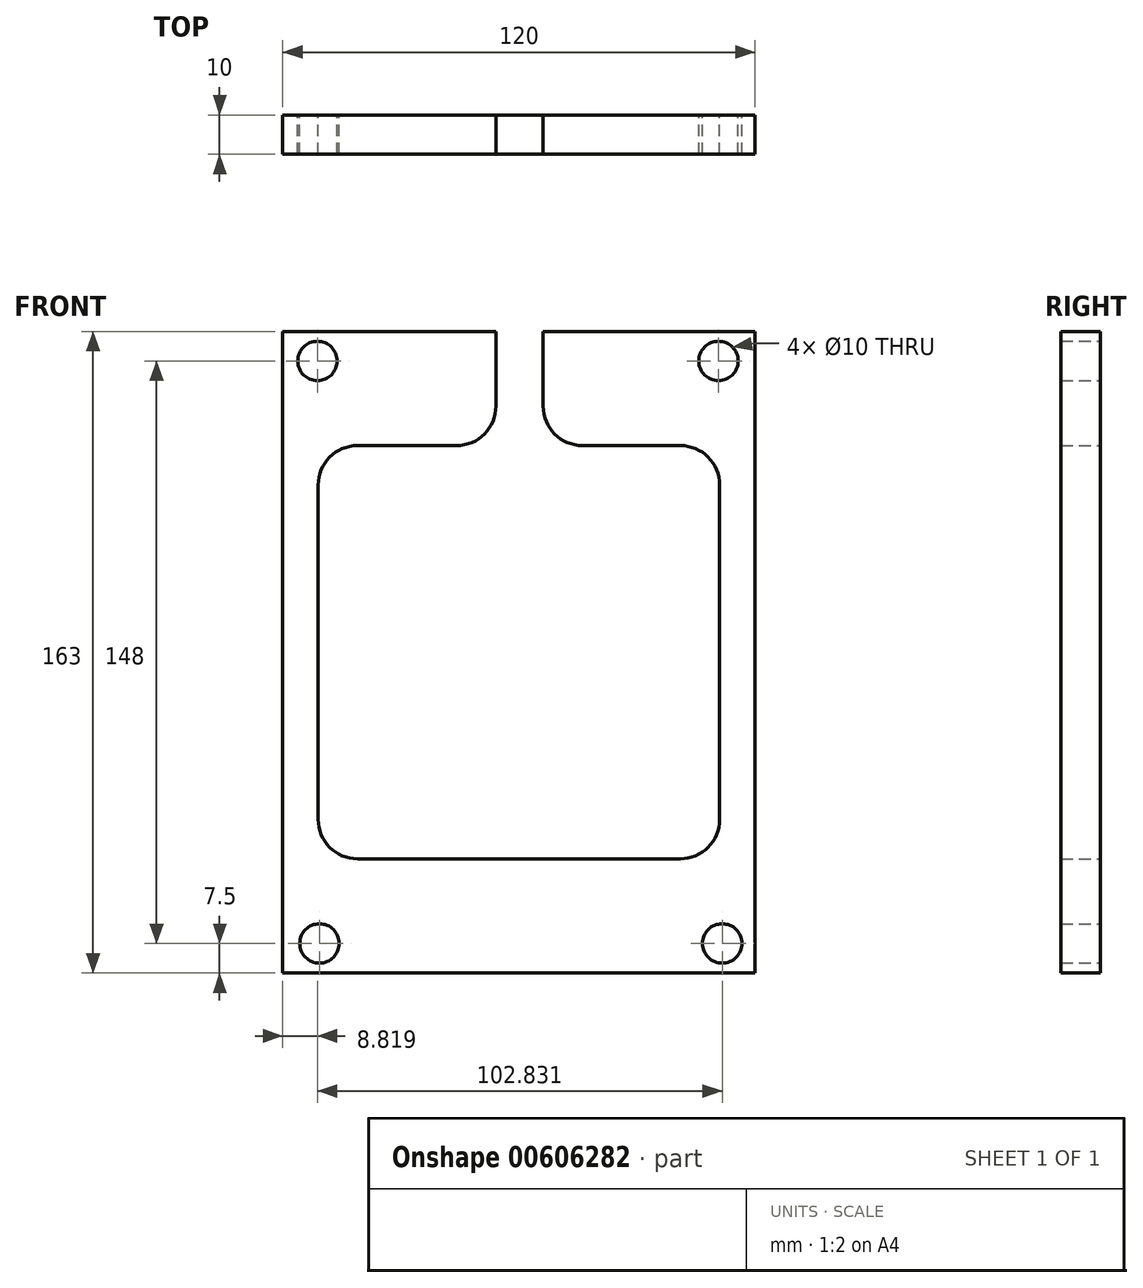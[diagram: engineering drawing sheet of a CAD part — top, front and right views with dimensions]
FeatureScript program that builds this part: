
annotation { "Feature Type Name" : "Feature", "Feature Type Description" : "" }
export const myFeature = defineFeature(function(context is Context, id is Id, definition is map)
    precondition{}
    {
        {
            var Q0;
            Q0=qCreatedBy(makeId("Front.planeOp"),FACE);
            var sketch = newSketch(context, id + "F0", { "sketchPlane" : qUnion([Q0])});
            skLineSegment(sketch, "E0.bottom", {"start": v(60, -81.5) * mm, "end": v(-60, -81.5) * mm});
            skLineSegment(sketch, "E0.top", {"start": v(60, 81.5) * mm, "end": v(-60, 81.5) * mm});
            skLineSegment(sketch, "E0.left", {"start": v(60, -81.5) * mm, "end": v(60, 81.5) * mm});
            skLineSegment(sketch, "E0.right", {"start": v(-60, -81.5) * mm, "end": v(-60, 81.5) * mm});
            skPoint(sketch, "E0.middle", {"position": v(0, 0) * mm});
            skLineSegment(sketch, "E1.bottom", {"start": v(41, -52.5) * mm, "end": v(-41, -52.5) * mm});
            skLineSegment(sketch, "E1.top", {"start": v(41, 52.5) * mm, "end": v(-41, 52.5) * mm});
            skLineSegment(sketch, "E1.left", {"start": v(51, -42.5) * mm, "end": v(51, 42.5) * mm});
            skLineSegment(sketch, "E1.right", {"start": v(-51, -42.5) * mm, "end": v(-51, 42.5) * mm});
            skPoint(sketch, "E2.visualSharp", {"position": v(-51, 52.5) * mm});
            skArc(sketch, "E2.filletArc", {"start": v(-41, 52.5) * mm, "mid": v(-48.07, 49.57) * mm, "end": v(-51, 42.5) * mm});
            skPoint(sketch, "E3.visualSharp", {"position": v(51, 52.5) * mm});
            skArc(sketch, "E3.filletArc", {"start": v(51, 42.5) * mm, "mid": v(48.07, 49.57) * mm, "end": v(41, 52.5) * mm});
            skPoint(sketch, "E4.visualSharp", {"position": v(51, -52.5) * mm});
            skArc(sketch, "E4.filletArc", {"start": v(41, -52.5) * mm, "mid": v(48.07, -49.57) * mm, "end": v(51, -42.5) * mm});
            skPoint(sketch, "E5.visualSharp", {"position": v(-51, -52.5) * mm});
            skArc(sketch, "E5.filletArc", {"start": v(-51, -42.5) * mm, "mid": v(-48.07, -49.57) * mm, "end": v(-41, -52.5) * mm});
            skLineSegment(sketch, "E6.bottom", {"start": v(-5.83, 52.5) * mm, "end": v(6.17, 52.5) * mm});
            skLineSegment(sketch, "E6.top", {"start": v(-5.83, 81.5) * mm, "end": v(6.17, 81.5) * mm});
            skLineSegment(sketch, "E6.left", {"start": v(-5.83, 52.5) * mm, "end": v(-5.83, 81.5) * mm});
            skLineSegment(sketch, "E6.right", {"start": v(6.17, 52.5) * mm, "end": v(6.17, 81.5) * mm});
            skCircle(sketch, "E7", {"center": v(-51.18, 74) * mm, "radius": 5 * mm});
            skCircle(sketch, "E8", {"center": v(50.7, 74) * mm, "radius": 5 * mm});
            skCircle(sketch, "E9", {"center": v(51.65, -74) * mm, "radius": 5 * mm});
            skCircle(sketch, "E10", {"center": v(-50.68, -74) * mm, "radius": 5 * mm});
            skSolve(sketch);
        }
        {
            var Q0;
            Q0=makeQuery(id+"F0.imprint","IMPRINT",FACE,{"disambiguationData":[TD([[makeQuery(id+"F0.imprint","IMPRINT",EDGE,{"derivedFrom":sQuery(id+"F0.wireOp",EDGE,"E0.bottom")}),-1.0]])]});
            extrude(context, id + "F1", {"entities" : qUnion([Q0]), "depth" : 10 * mm, "offsetDistance" : 25 * mm});
        }
        {
            var Q0;
            Q0=makeQuery(id+"F1.opExtrude","SWEPT_EDGE",EDGE,{"disambiguationData":[OSD([sQuery(id+"F0.wireOp",EDGE,"E1.top"),sQuery(id+"F0.wireOp",EDGE,"E6.bottom"),sQuery(id+"F0.wireOp",EDGE,"E6.left")])]});
            fillet(context, id + "F2", {"entities" : qUnion([Q0]), "radius" : 10 * mm, "tangentPropagation" : true, "allowEdgeOverflow" : false});
        }
        {
            var Q0;
            Q0=makeQuery(id+"F1.opExtrude","SWEPT_EDGE",EDGE,{"disambiguationData":[OSD([sQuery(id+"F0.wireOp",EDGE,"E1.top"),sQuery(id+"F0.wireOp",EDGE,"E6.bottom"),sQuery(id+"F0.wireOp",EDGE,"E6.right")])]});
            fillet(context, id + "F3", {"entities" : qUnion([Q0]), "radius" : 10 * mm, "tangentPropagation" : true, "allowEdgeOverflow" : false});
        }
    });
